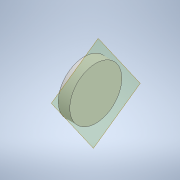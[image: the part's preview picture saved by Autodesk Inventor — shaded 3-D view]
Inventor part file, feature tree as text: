
AUTODESK INVENTOR PART (.ipt)
format: ipt  version: 2020 (Build 240168000, 168)  size: 122,880 bytes
history: native  units: mm
features: other x3, extrude x2, sketch x2, plane x1, reference x1, projected_geometry x1
ambient origin geometry x8: Origin, YZ Plane, XZ Plane, XY Plane, X Axis, Y Axis, Z Axis, Center Point
bodies: Solid1 (feature_tree)
feature tree (10):
  plane  "Work Plane1"
  extrude  "Extrusion1"  Depth=1.0mm TaperAngle=0.0deg
  extrude  "Extrusion2"  [1 undecoded]
  sketch  "Sketch1"  dims[d0=7.327mm d1=0.0mm d2=1.0mm d3=0.0mm]
  reference  "Reference1"
  sketch  "Sketch2"
  projected_geometry  "Projected Loop1"
  other  "<userpath>\Documents\Inventor\CC_RENEV\belzebub.iam"
  other  "belzebub.iam"
  other  "Part5:1"
note: 1 required parameter value undecoded (feature->parameter linkage not recoverable at this tier; creation-order binding heuristic only, values carry confidence <= 0.55)
